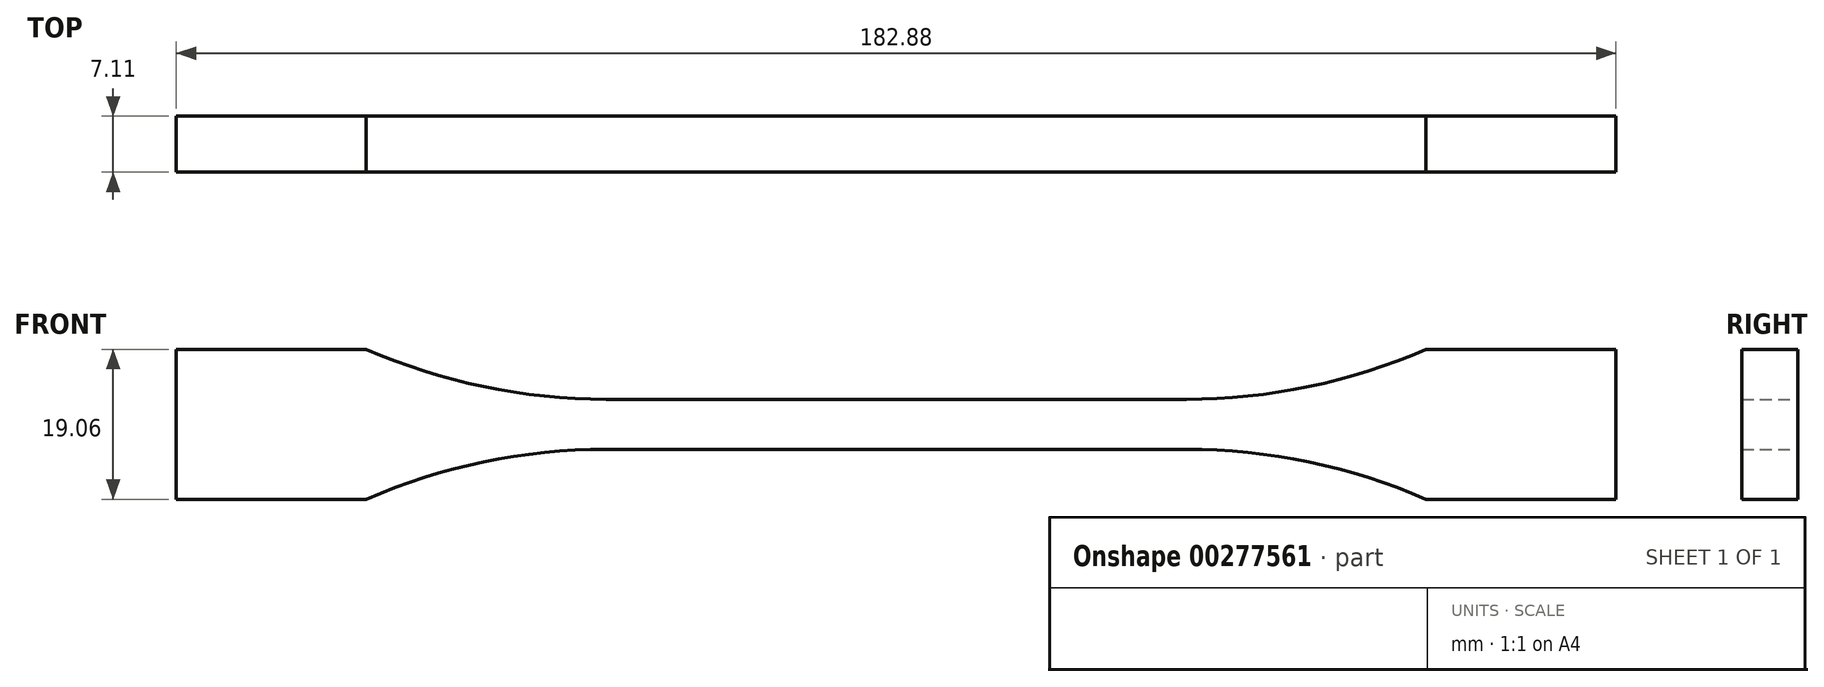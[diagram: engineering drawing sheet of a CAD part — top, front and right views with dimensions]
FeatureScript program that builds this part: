
annotation { "Feature Type Name" : "Feature", "Feature Type Description" : "" }
export const myFeature = defineFeature(function(context is Context, id is Id, definition is map)
    precondition{}
    {
        {
            var Q0;
            Q0=qCreatedBy(makeId("Front.planeOp"),FACE);
            var sketch = newSketch(context, id + "F0", { "sketchPlane" : qUnion([Q0])});
            skLineSegment(sketch, "E0", {"start": v(0, 3.18) * mm, "end": v(36.86, 3.18) * mm});
            skArc(sketch, "E1", {"start": v(36.86, 3.17) * mm, "mid": v(52.41, 4.78) * mm, "end": v(67.31, 9.53) * mm});
            skLineSegment(sketch, "E2", {"start": v(67.31, 9.53) * mm, "end": v(91.44, 9.53) * mm});
            skLineSegment(sketch, "E3", {"start": v(91.44, 9.53) * mm, "end": v(91.44, 0) * mm});
            skLineSegment(sketch, "E4.MirrorCS", {"start": v(0, -3.18) * mm, "end": v(36.86, -3.18) * mm});
            skLineSegment(sketch, "E5.MirrorCS", {"start": v(91.44, -9.53) * mm, "end": v(91.44, 0) * mm});
            skLineSegment(sketch, "E6.MirrorCS", {"start": v(67.31, -9.52) * mm, "end": v(91.44, -9.52) * mm});
            skArc(sketch, "E7.MirrorCS", {"start": v(36.86, -3.17) * mm, "mid": v(52.41, -4.78) * mm, "end": v(67.31, -9.53) * mm});
            skArc(sketch, "E8.MirrorCS", {"start": v(-36.86, -3.17) * mm, "mid": v(-52.41, -4.78) * mm, "end": v(-67.31, -9.53) * mm});
            skLineSegment(sketch, "E9.MirrorCS", {"start": v(-67.31, -9.53) * mm, "end": v(-91.44, -9.53) * mm});
            skArc(sketch, "E10.MirrorCS", {"start": v(-36.86, 3.17) * mm, "mid": v(-52.41, 4.78) * mm, "end": v(-67.31, 9.53) * mm});
            skLineSegment(sketch, "E11.MirrorCS", {"start": v(-67.31, 9.52) * mm, "end": v(-91.44, 9.52) * mm});
            skLineSegment(sketch, "E12.MirrorCS", {"start": v(-91.44, -9.53) * mm, "end": v(-91.44, 0) * mm});
            skLineSegment(sketch, "E13.MirrorCS", {"start": v(0, -3.18) * mm, "end": v(-36.86, -3.18) * mm});
            skLineSegment(sketch, "E14.MirrorCS", {"start": v(-91.44, 9.53) * mm, "end": v(-91.44, 0) * mm});
            skLineSegment(sketch, "E15.MirrorCS", {"start": v(0, 3.18) * mm, "end": v(-36.86, 3.18) * mm});
            skSolve(sketch);
        }
        {
            var Q0;
            Q0 = qSketchRegion(id + "F0", true);
            extrude(context, id + "F1", {"entities" : qUnion([Q0]), "depth" : 7.11 * mm});
        }
    });
